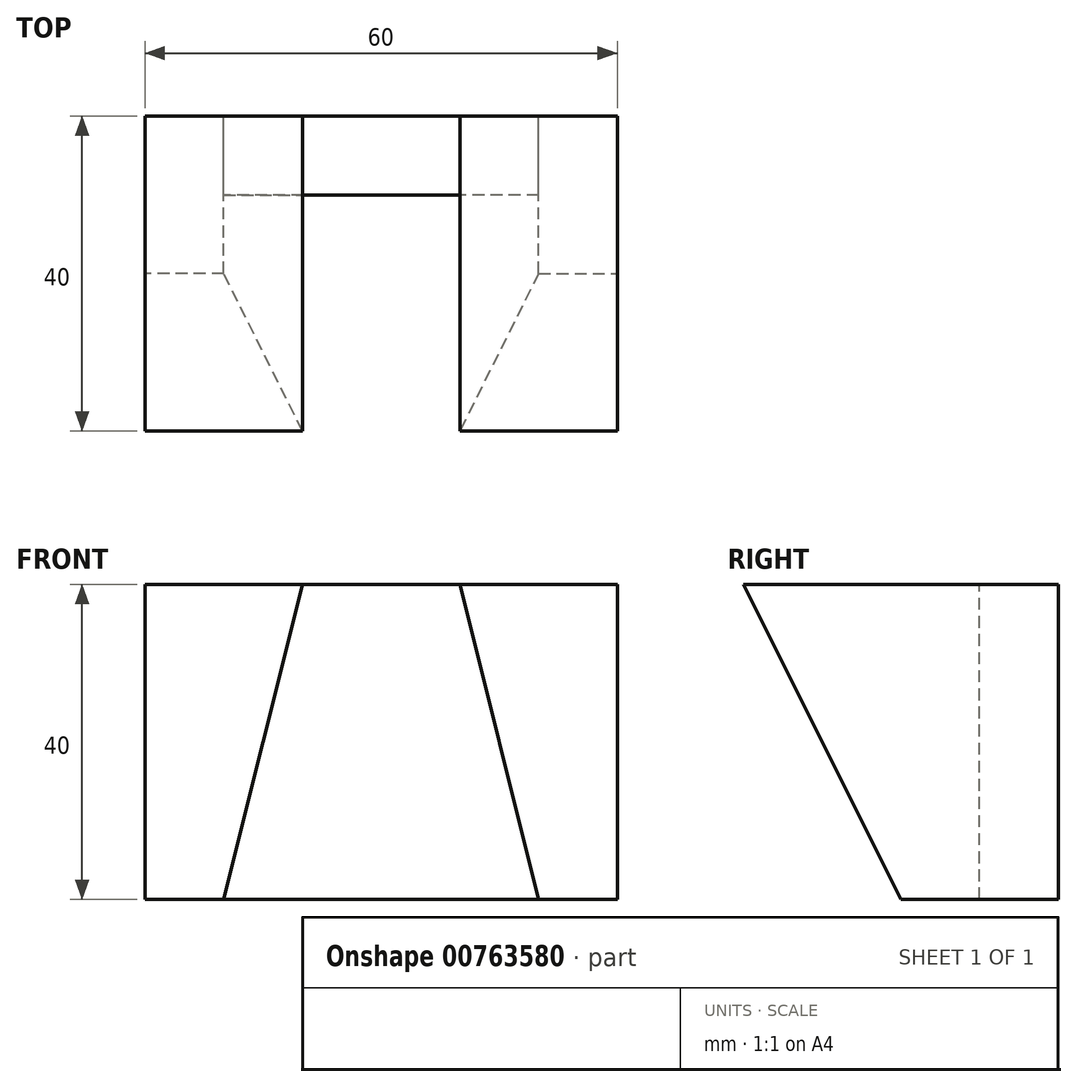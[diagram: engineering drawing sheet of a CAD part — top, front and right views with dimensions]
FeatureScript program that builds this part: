
annotation { "Feature Type Name" : "Feature", "Feature Type Description" : "" }
export const myFeature = defineFeature(function(context is Context, id is Id, definition is map)
    precondition{}
    {
        {
            var Q0;
            Q0=qCreatedBy(makeId("Front.planeOp"),FACE);
            var sketch = newSketch(context, id + "F0", { "sketchPlane" : qUnion([Q0])});
            skLineSegment(sketch, "E0", {"start": v(-20, 0) * mm, "end": v(-10, 0) * mm});
            skLineSegment(sketch, "E1", {"start": v(-10, 0) * mm, "end": v(0, 40) * mm});
            skLineSegment(sketch, "E2", {"start": v(0, 40) * mm, "end": v(-20, 40) * mm});
            skLineSegment(sketch, "E3", {"start": v(-20, 40) * mm, "end": v(-20, 0) * mm});
            skLineSegment(sketch, "E4", {"start": v(-20, 40) * mm, "end": v(40, 40) * mm});
            skLineSegment(sketch, "E5", {"start": v(40, 40) * mm, "end": v(40, 0) * mm});
            skLineSegment(sketch, "E6", {"start": v(40, 0) * mm, "end": v(-10, 0) * mm});
            skLineSegment(sketch, "E7", {"start": v(40, 40) * mm, "end": v(20, 40) * mm});
            skLineSegment(sketch, "E8", {"start": v(40, 0) * mm, "end": v(30, 0) * mm});
            skLineSegment(sketch, "E9", {"start": v(30, 0) * mm, "end": v(20, 40) * mm});
            skSolve(sketch);
        }
        {
            var Q0;
            Q0=makeQuery(id+"F0.imprint","IMPRINT",FACE,{"disambiguationData":[TD([[makeQuery(id+"F0.imprint","IMPRINT",EDGE,{"derivedFrom":sQuery(id+"F0.wireOp",EDGE,"E0")}),1.0]])]});
            extrude(context, id + "F1", {"entities" : qUnion([Q0]), "depth" : 40 * mm, "offsetDistance" : 25 * mm});
        }
        {
            var Q0;
            Q0=makeQuery(id+"F0.imprint","IMPRINT",FACE,{"disambiguationData":[TD([[makeQuery(id+"F0.imprint","IMPRINT",EDGE,{"derivedFrom":sQuery(id+"F0.wireOp",EDGE,"E5")}),-1.0]])]});
            extrude(context, id + "F2", {"entities" : qUnion([Q0]), "depth" : 40 * mm, "offsetDistance" : 25 * mm});
        }
        {
            var Q0;
            {var subQ0=sQuery(id+"F0.wireOp",EDGE,"E1");Q0=makeQuery(id+"F0.imprint","IMPRINT",FACE,{"disambiguationData":[TD([[makeQuery(id+"F0.imprint","IMPRINT",EDGE,{"derivedFrom":subQ0}),-1.0]])]});}
            extrude(context, id + "F3", {"entities" : qUnion([Q0]), "depth" : 10 * mm, "offsetDistance" : 25 * mm});
        }
        {
            var Q0;
            Q0=makeQuery(id+"F1.opExtrude","SWEPT_FACE",FACE,{"disambiguationData":[OSD([sQuery(id+"F0.wireOp",EDGE,"E3")])]});
            var sketch = newSketch(context, id + "F4", { "sketchPlane" : qUnion([Q0])});
            skLineSegment(sketch, "E10", {"start": v(0, 0) * mm, "end": v(10, 0) * mm});
            skLineSegment(sketch, "E11", {"start": v(10, 0) * mm, "end": v(20, 0) * mm});
            skLineSegment(sketch, "E12", {"start": v(20, 0) * mm, "end": v(30, 0) * mm});
            skLineSegment(sketch, "E13", {"start": v(30, 0) * mm, "end": v(40, 0) * mm});
            skLineSegment(sketch, "E14", {"start": v(40, 40) * mm, "end": v(20, 0) * mm});
            skSolve(sketch);
        }
        {
            var Q0;
            Q0=makeQuery(id+"F4.imprint","IMPRINT",FACE,{"disambiguationData":[TD([[makeQuery(id+"F4.imprint","IMPRINT",EDGE,{"derivedFrom":sQuery(id+"F4.wireOp",EDGE,"E12")}),-1.0]])]});
            extrude(context, id + "F5", {"entities" : qUnion([Q0]), "operationType" : NewBodyOperationType.REMOVE, "oppositeDirection" : true, "depth" : 25 * mm, "offsetDistance" : 25 * mm});
        }
        {
            var Q0;
            Q0=makeQuery(id+"F2.opExtrude","SWEPT_FACE",FACE,{"disambiguationData":[OSD([sQuery(id+"F0.wireOp",EDGE,"E5")])]});
            var sketch = newSketch(context, id + "F6", { "sketchPlane" : qUnion([Q0])});
            skLineSegment(sketch, "E15", {"start": v(0, 0) * mm, "end": v(-10, 0) * mm});
            skLineSegment(sketch, "E16", {"start": v(-10, 0) * mm, "end": v(-20, 0) * mm});
            skLineSegment(sketch, "E17", {"start": v(-20, 0) * mm, "end": v(-30, 0) * mm});
            skLineSegment(sketch, "E18", {"start": v(-30, 0) * mm, "end": v(-40, 0) * mm});
            skLineSegment(sketch, "E19", {"start": v(-40, 40) * mm, "end": v(-20, 0) * mm});
            skSolve(sketch);
        }
        {
            var Q0;
            Q0=makeQuery(id+"F6.imprint","IMPRINT",FACE,{"disambiguationData":[TD([[makeQuery(id+"F6.imprint","IMPRINT",EDGE,{"derivedFrom":sQuery(id+"F6.wireOp",EDGE,"E17")}),1.0]])]});
            extrude(context, id + "F7", {"entities" : qUnion([Q0]), "operationType" : NewBodyOperationType.REMOVE, "oppositeDirection" : true, "depth" : 25 * mm, "offsetDistance" : 25 * mm});
        }
    });
